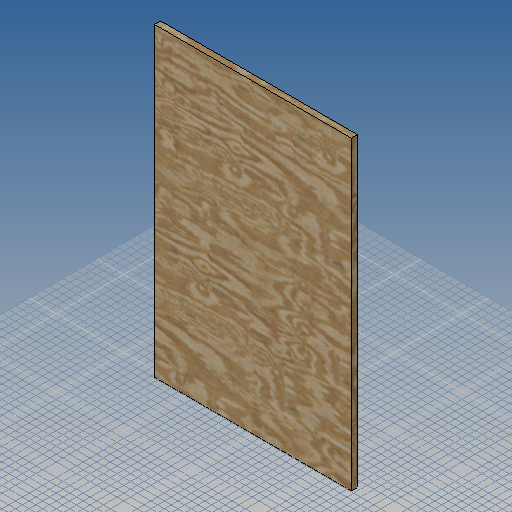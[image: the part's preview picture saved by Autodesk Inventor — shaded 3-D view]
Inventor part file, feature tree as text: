
AUTODESK INVENTOR PART (.ipt)
format: ipt  version: 2019 (Build 230136000, 136)  size: 283,136 bytes
history: native  units: mm
features: other x1, extrude x1, sketch x1
ambient origin geometry x8: Origin, YZ Plane, XZ Plane, XY Plane, X Axis, Y Axis, Z Axis, Center Point
bodies: Volumenkörper1 (feature_tree)
feature tree (3):
  other  "<userpath>\OneDrive\Dokumente\Inventor\Absauganlage\Absauganlage_Params.xlsx"
  extrude  "Extrusion1"  Depth=904.0mm
  sketch  "Skizze1"  dims[d0=582.0mm d1=904.0mm d2=18.0mm d3=0.0mm]
